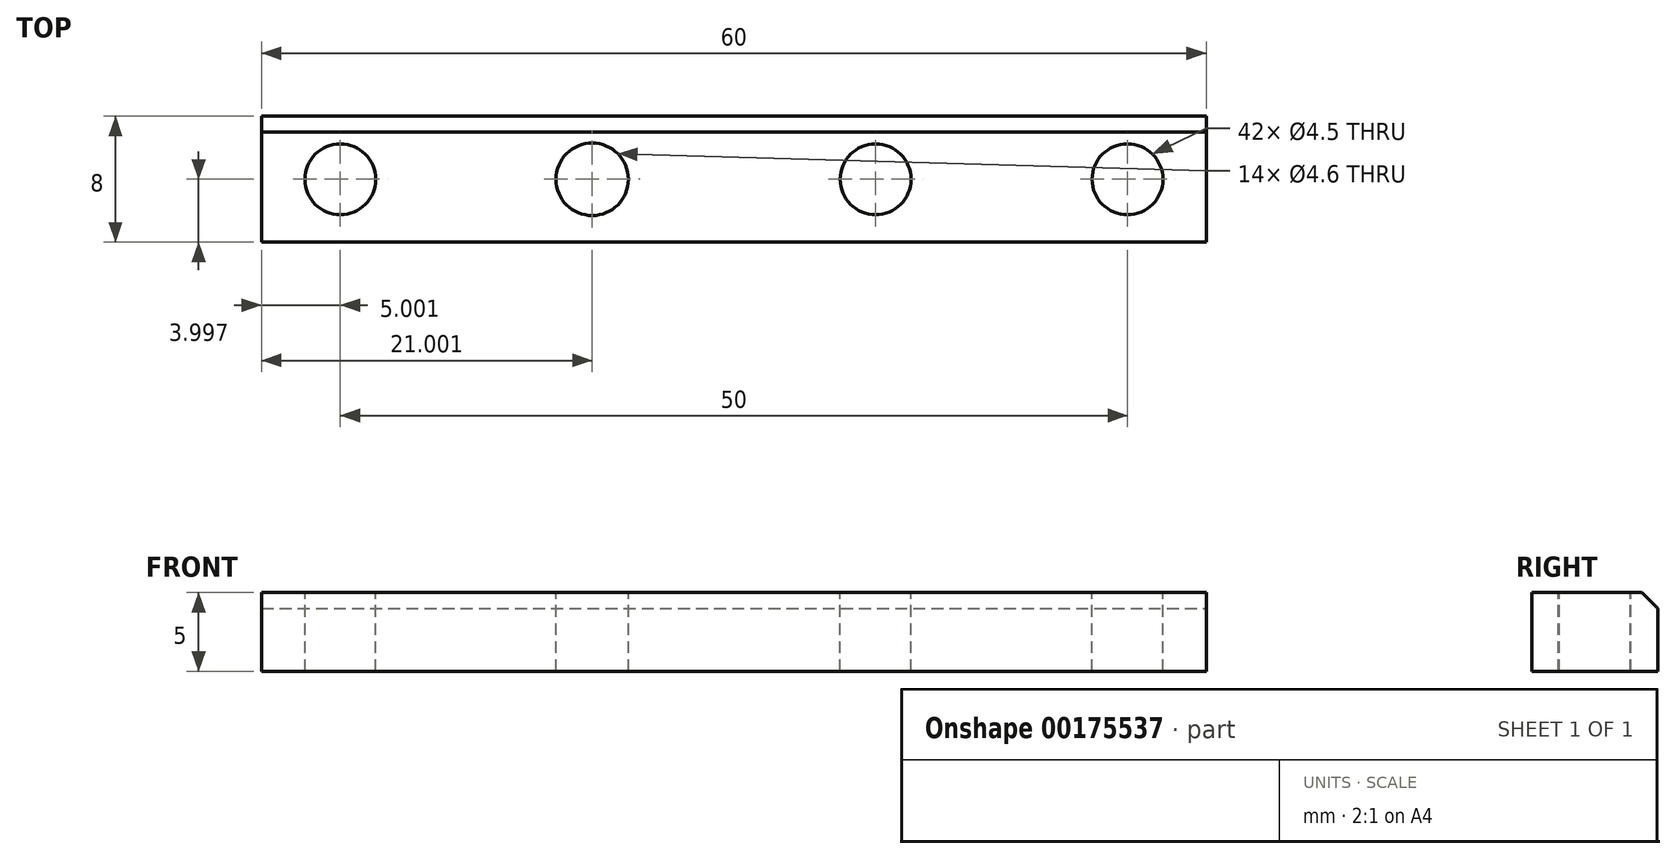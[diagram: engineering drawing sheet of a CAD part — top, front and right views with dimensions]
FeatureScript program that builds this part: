
annotation { "Feature Type Name" : "Feature", "Feature Type Description" : "" }
export const myFeature = defineFeature(function(context is Context, id is Id, definition is map)
    precondition{}
    {
        {
            var Q0;
            Q0=qCreatedBy(makeId("Top.planeOp"),FACE);
            var sketch = newSketch(context, id + "F0", { "sketchPlane" : qUnion([Q0])});
            skLineSegment(sketch, "E0.bottom", {"start": v(-29.23, -7.36) * mm, "end": v(30.77, -7.36) * mm});
            skLineSegment(sketch, "E0.top", {"start": v(-29.23, 0.64) * mm, "end": v(30.77, 0.64) * mm});
            skLineSegment(sketch, "E0.left", {"start": v(-29.23, -7.36) * mm, "end": v(-29.23, 0.64) * mm});
            skLineSegment(sketch, "E0.right", {"start": v(30.77, -7.36) * mm, "end": v(30.77, 0.64) * mm});
            skSolve(sketch);
        }
        {
            var Q0;
            Q0=qSketchRegion(id+"F0",true);
            extrude(context, id + "F1", {"entities" : qUnion([Q0]), "depth" : 5 * mm});
        }
        {
            var Q0;
            Q0=makeQuery(id+"F1.opExtrude","CAP_FACE",FACE,{"disambiguationData":[OSD([sQuery(id+"F0.wireOp",EDGE,"E0.bottom"),sQuery(id+"F0.wireOp",EDGE,"E0.top"),sQuery(id+"F0.wireOp",EDGE,"E0.left"),sQuery(id+"F0.wireOp",EDGE,"E0.right")])],"isStart":false});
            var sketch = newSketch(context, id + "F2", { "sketchPlane" : qUnion([Q0])});
            skLineSegment(sketch, "E1", {"start": v(-29.23, -3.36) * mm, "end": v(30.77, -3.36) * mm, "construction": true});
            skCircle(sketch, "E2", {"center": v(-8.23, -3.36) * mm, "radius": 2.3 * mm});
            skCircle(sketch, "E3", {"center": v(9.77, -3.36) * mm, "radius": 2.25 * mm});
            skCircle(sketch, "E4", {"center": v(25.77, -3.36) * mm, "radius": 2.25 * mm});
            skCircle(sketch, "E5", {"center": v(-24.23, -3.36) * mm, "radius": 2.25 * mm});
            skLineSegment(sketch, "E6", {"start": v(0.77, -7.36) * mm, "end": v(0.77, 0.64) * mm, "construction": true});
            skSolve(sketch);
        }
        {
            var Q0;
            Q0=qSketchRegion(id+"F2",true);
            extrude(context, id + "F3", {"entities" : qUnion([Q0]), "operationType" : NewBodyOperationType.REMOVE, "endBound" : BoundingType.THROUGH_ALL, "oppositeDirection" : true, "depth" : 25 * mm});
        }
        {
            var Q0;
            Q0=makeQuery(id+"F1.opExtrude","CAP_EDGE",EDGE,{"disambiguationData":[OSD([sQuery(id+"F0.wireOp",EDGE,"E0.top")])],"isStart":false});
            chamfer(context, id + "F4", {"entities" : qUnion([Q0]), "width" : 1 * mm, "tangentPropagation" : true});
        }
    });
